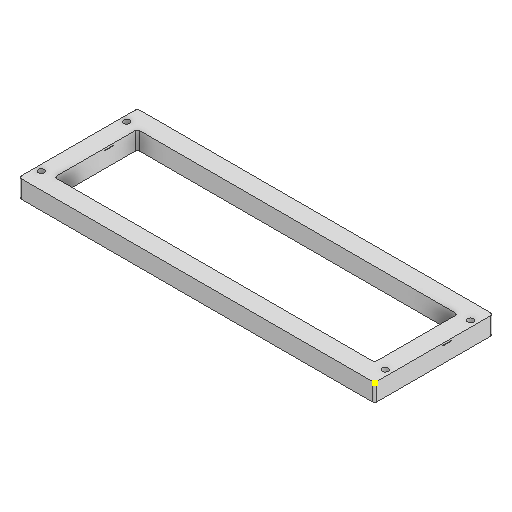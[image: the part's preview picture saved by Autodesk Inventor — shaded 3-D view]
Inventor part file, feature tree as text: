
AUTODESK INVENTOR PART (.ipt)
format: ipt  version: 2025.1 (Build 291241000, 241)  size: 147,968 bytes
history: native  units: mm
features: sketch x5, extrude x3, other x1, fillet x1, hole x1
ambient origin geometry x8: Origin, YZ Plane, XZ Plane, XY Plane, X Axis, Y Axis, Z Axis, Center Point
bodies: Body1 (feature_tree)
feature tree (11):
  other  "Bryła1"
  sketch  "Szkic1"
  sketch  "Szkic2"
  extrude  "Wyciągnięcie proste1"  Depth=100.0mm
  extrude  "Wyciągnięcie proste2"  Depth=300.0mm
  fillet  "Zaokrąglenie1"  Radius=270.0mm
  hole  "Otwór1"  [1 undecoded]
  sketch  "Szkic4"
  extrude  "Wyciągnięcie proste3"  Depth=15.0mm
  sketch  "Szkic3"
  sketch  "Szkic5"
note: 1 required parameter value undecoded (feature->parameter linkage not recoverable at this tier; creation-order binding heuristic only, values carry confidence <= 0.55)
